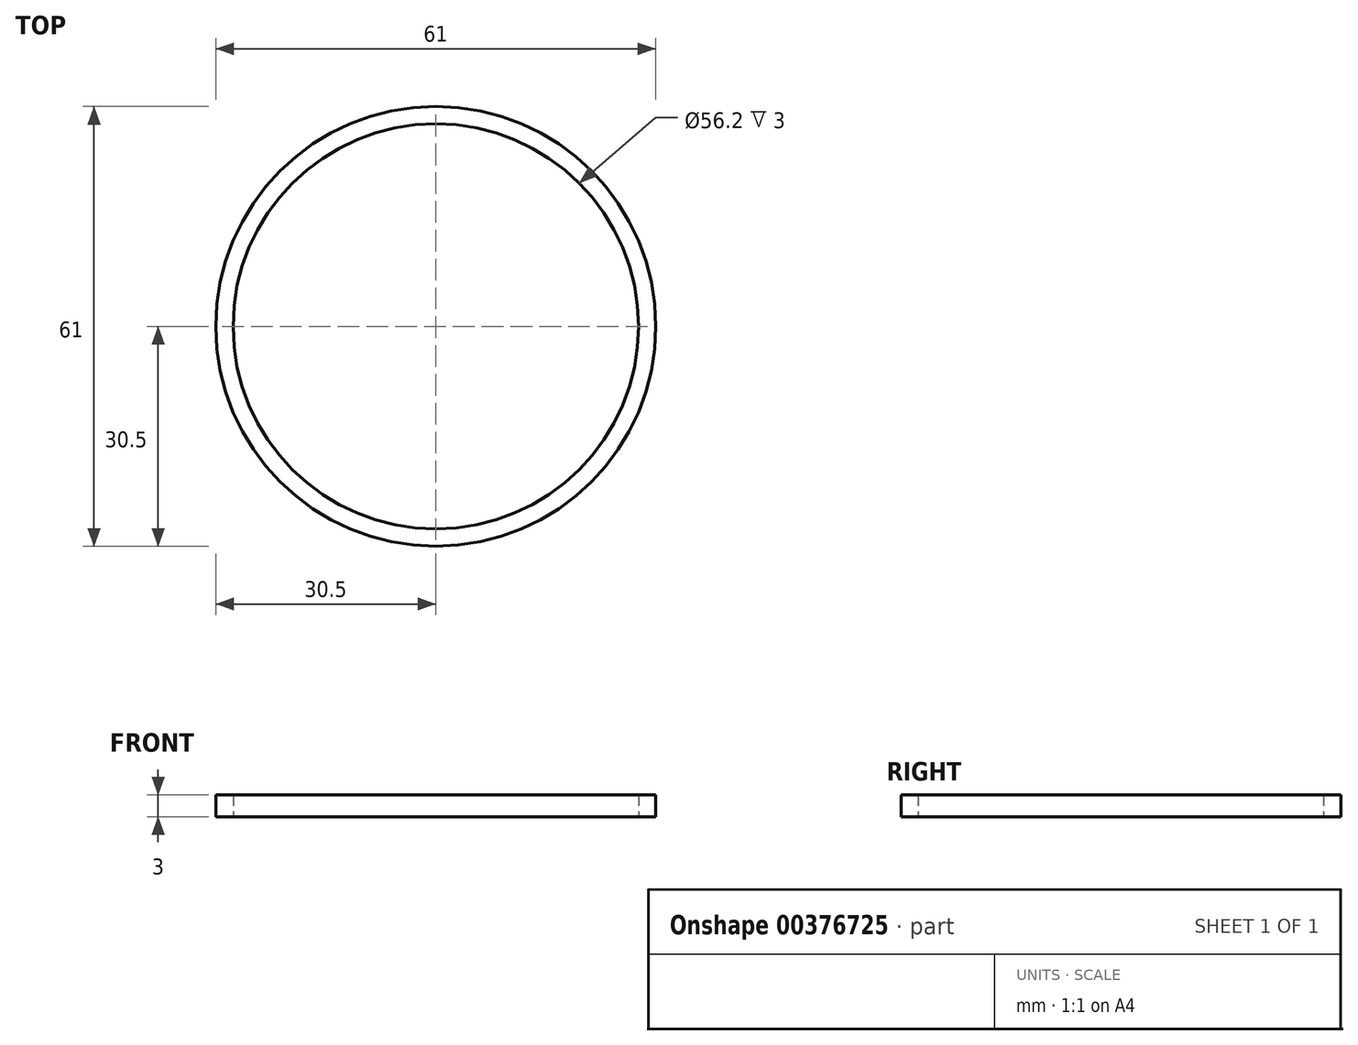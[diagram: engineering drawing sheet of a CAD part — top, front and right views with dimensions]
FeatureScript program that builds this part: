
annotation { "Feature Type Name" : "Feature", "Feature Type Description" : "" }
export const myFeature = defineFeature(function(context is Context, id is Id, definition is map)
    precondition{}
    {
        {
            var Q0;
            Q0=qCreatedBy(makeId("Top.planeOp"),FACE);
            var sketch = newSketch(context, id + "F0", { "sketchPlane" : qUnion([Q0])});
            skCircle(sketch, "E0", {"center": v(0, 0) * mm, "radius": 30.5 * mm});
            skCircle(sketch, "E1", {"center": v(0, 0) * mm, "radius": 28.1 * mm});
            skSolve(sketch);
        }
        {
            var Q0;
            Q0=makeQuery(id+"F0.imprint","IMPRINT",FACE,{"disambiguationData":[TD([[makeQuery(id+"F0.imprint","IMPRINT",EDGE,{"derivedFrom":sQuery(id+"F0.wireOp",EDGE,"E0")}),1.0]])]});
            extrude(context, id + "F1", {"entities" : qUnion([Q0]), "depth" : 3 * mm});
        }
    });
